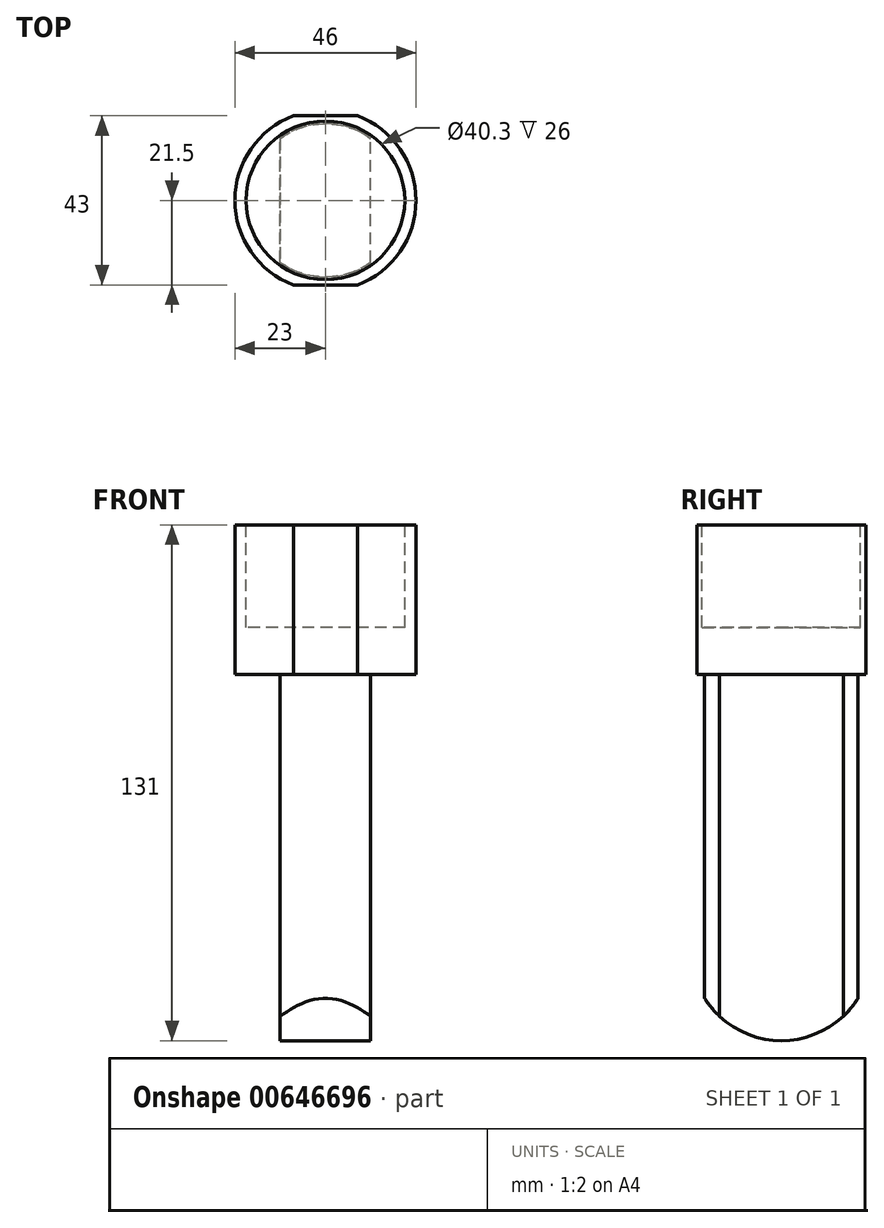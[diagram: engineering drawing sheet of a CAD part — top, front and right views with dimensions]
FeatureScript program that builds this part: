
annotation { "Feature Type Name" : "Feature", "Feature Type Description" : "" }
export const myFeature = defineFeature(function(context is Context, id is Id, definition is map)
    precondition{}
    {
        {
            var Q0;
            Q0=qCreatedBy(makeId("Top.planeOp"),FACE);
            var sketch = newSketch(context, id + "F0", { "sketchPlane" : qUnion([Q0])});
            skArc(sketch, "E0", {"start": v(-8.17, 21.5) * mm, "mid": v(-23, 0) * mm, "end": v(-8.17, -21.5) * mm});
            skLineSegment(sketch, "E1", {"start": v(-8.17, 21.5) * mm, "end": v(8.17, 21.5) * mm});
            skLineSegment(sketch, "E2.MirrorCS", {"start": v(-8.17, -21.5) * mm, "end": v(8.17, -21.5) * mm});
            skArc(sketch, "E3.trimOffspring", {"start": v(8.17, -21.5) * mm, "mid": v(23, 0) * mm, "end": v(8.17, 21.5) * mm});
            skSolve(sketch);
        }
        {
            var Q0;
            Q0=makeQuery(id+"F0.imprint","IMPRINT",FACE,{"disambiguationData":[TD([[makeQuery(id+"F0.imprint","IMPRINT",EDGE,{"derivedFrom":sQuery(id+"F0.wireOp",EDGE,"E0")}),1.0]])]});
            extrude(context, id + "F1", {"entities" : qUnion([Q0]), "depth" : 38 * mm, "offsetDistance" : 25 * mm});
        }
        {
            var Q0;
            Q0=makeQuery(id+"F1.opExtrude","CAP_FACE",FACE,{"disambiguationData":[OSD([sQuery(id+"F0.wireOp",EDGE,"E0"),sQuery(id+"F0.wireOp",EDGE,"E1"),sQuery(id+"F0.wireOp",EDGE,"E2.MirrorCS"),sQuery(id+"F0.wireOp",EDGE,"E3.trimOffspring")])],"isStart":false});
            var sketch = newSketch(context, id + "F2", { "sketchPlane" : qUnion([Q0])});
            skCircle(sketch, "E4", {"center": v(0, 0) * mm, "radius": 20.15 * mm});
            skSolve(sketch);
        }
        {
            var Q0;
            Q0=makeQuery(id+"F2.imprint","IMPRINT",FACE,{"disambiguationData":[TD([[makeQuery(id+"F2.imprint","IMPRINT",EDGE,{"derivedFrom":sQuery(id+"F2.wireOp",EDGE,"E4")}),1.0]])]});
            extrude(context, id + "F3", {"entities" : qUnion([Q0]), "operationType" : NewBodyOperationType.REMOVE, "oppositeDirection" : true, "depth" : 26 * mm, "offsetDistance" : 25 * mm});
        }
        {
            var Q0;
            Q0=makeQuery(id+"F1.opExtrude","CAP_FACE",FACE,{"disambiguationData":[OSD([sQuery(id+"F0.wireOp",EDGE,"E0"),sQuery(id+"F0.wireOp",EDGE,"E1"),sQuery(id+"F0.wireOp",EDGE,"E2.MirrorCS"),sQuery(id+"F0.wireOp",EDGE,"E3.trimOffspring")])],"isStart":true});
            var sketch = newSketch(context, id + "F4", { "sketchPlane" : qUnion([Q0])});
            skArc(sketch, "E5", {"start": v(-11.5, -15.75) * mm, "mid": v(0, -19.5) * mm, "end": v(11.5, -15.75) * mm});
            skLineSegment(sketch, "E6", {"start": v(-11.5, 15.75) * mm, "end": v(-11.5, -15.75) * mm});
            skLineSegment(sketch, "E7.MirrorCS", {"start": v(11.5, 15.75) * mm, "end": v(11.5, -15.75) * mm});
            skArc(sketch, "E8.trimOffspring", {"start": v(11.5, 15.75) * mm, "mid": v(0, 19.5) * mm, "end": v(-11.5, 15.75) * mm});
            skSolve(sketch);
        }
        {
            var Q0;
            Q0=makeQuery(id+"F4.imprint","IMPRINT",FACE,{"disambiguationData":[TD([[makeQuery(id+"F4.imprint","IMPRINT",EDGE,{"derivedFrom":sQuery(id+"F4.wireOp",EDGE,"E5")}),1.0]])]});
            extrude(context, id + "F5", {"entities" : qUnion([Q0]), "operationType" : NewBodyOperationType.ADD, "depth" : 93 * mm, "offsetDistance" : 25 * mm});
        }
        {
            var Q0;
            Q0=makeQuery(id+"F5.opExtrude","SWEPT_FACE",FACE,{"disambiguationData":[OSD([sQuery(id+"F4.wireOp",EDGE,"E6")])]});
            var sketch = newSketch(context, id + "F6", { "sketchPlane" : qUnion([Q0])});
            skArc(sketch, "E9", {"start": v(-23, -70.19) * mm, "mid": v(-0.33, -93) * mm, "end": v(22.98, -70.84) * mm});
            skLineSegment(sketch, "E10", {"start": v(-23, -70.19) * mm, "end": v(-39.57, -112.17) * mm});
            skLineSegment(sketch, "E11", {"start": v(-39.57, -112.17) * mm, "end": v(46.8, -112.17) * mm});
            skLineSegment(sketch, "E12", {"start": v(46.8, -112.17) * mm, "end": v(22.98, -70.84) * mm});
            skSolve(sketch);
        }
        {
            var Q0;
            {var subQ0=sQuery(id+"F6.wireOp",EDGE,"E9");var subQ1=sQuery(id+"F4.wireOp",EDGE,"E6");var subQ4=makeQuery(id+"F5.opExtrude","CAP_EDGE",EDGE,{"disambiguationData":[OSD([subQ1])],"isStart":false});var subQ5=makeQuery(id+"F6.imprint","INTERSECT",VERTEX,{"derivedFrom":[subQ4,subQ0]});Q0=makeQuery(id+"F6.imprint","IMPRINT",FACE,{"disambiguationData":[TD([[makeQuery(id+"F6.imprint","IMPRINT",EDGE,{"disambiguationData":[TD([[subQ5,1.0]])],"derivedFrom":subQ0}),-1.0]])]});}
            var Q1;
            {var subQ0=sQuery(id+"F6.wireOp",EDGE,"E9");var subQ1=sQuery(id+"F4.wireOp",EDGE,"E6");var subQ4=makeQuery(id+"F5.opExtrude","CAP_EDGE",EDGE,{"disambiguationData":[OSD([subQ1])],"isStart":false});var subQ5=makeQuery(id+"F6.imprint","INTERSECT",VERTEX,{"derivedFrom":[subQ4,subQ0]});Q1=makeQuery(id+"F6.imprint","IMPRINT",FACE,{"disambiguationData":[TD([[makeQuery(id+"F6.imprint","IMPRINT",EDGE,{"disambiguationData":[TD([[subQ5,-1.0]])],"derivedFrom":subQ0}),-1.0]])]});}
            var Q2;
            {var subQ0=sQuery(id+"F6.wireOp",EDGE,"E10");Q2=makeQuery(id+"F6.imprint","IMPRINT",FACE,{"disambiguationData":[TD([[makeQuery(id+"F6.imprint","IMPRINT",EDGE,{"derivedFrom":subQ0}),1.0]])]});}
            extrude(context, id + "F7", {"entities" : qUnion([Q0, Q1, Q2]), "operationType" : NewBodyOperationType.REMOVE, "oppositeDirection" : true, "depth" : 25 * mm, "offsetDistance" : 25 * mm});
        }
    });
